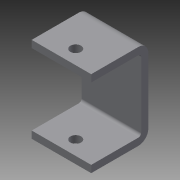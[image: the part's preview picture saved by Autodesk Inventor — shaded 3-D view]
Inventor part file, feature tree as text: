
AUTODESK INVENTOR PART (.ipt)
format: ipt  version: 2013 (Build 170138000, 138)  size: 115,200 bytes
history: native  units: in
note: dims shown in document units (in); Inventor stores cm internally (conversion verified against a paired STEP export)
features: sheet_metal_op x4, sketch x3, other x2, extrude x1
ambient origin geometry x8: Origin, YZ Plane, XZ Plane, XY Plane, X Axis, Y Axis, Z Axis, Center Point
bodies: Solid1 (feature_tree)
feature tree (10):
  sheet_metal_op  "Face1"
  sheet_metal_op  "Flange1"
  extrude  "Extrusion1"  Depth=1.15in
  sketch  "Sketch1"  dims[d4=0.5788in d5=1.15in]
  other  "Plate1"
  sketch  "Sketch2"  dims[d6=0.125in]
  other  "Plate2"
  sheet_metal_op  "Bend1"
  sheet_metal_op  "Corner1"
  sketch  "Sketch3"  dims[d7=0.125in d8=0.0625in d9=0.25in d10=0.125in d11=1.0in d12=90.0deg d13=0.05in d14=0.5in d15=0.125in d16=0.125in d17=0.25in d18=0.1875in d19=2999.0in d20=0.0in d21=0.575in]
